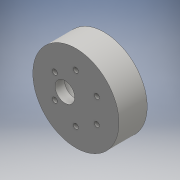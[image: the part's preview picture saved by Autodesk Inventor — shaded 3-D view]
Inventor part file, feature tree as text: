
AUTODESK INVENTOR PART (.ipt)
format: ipt  version: 2016 (Build 200138000, 138)  size: 124,416 bytes
history: native  units: mm
features: extrude x2, sketch x2
ambient origin geometry x8: Origin, YZ Plane, XZ Plane, XY Plane, X Axis, Y Axis, Z Axis, Center Point
bodies: Solid1 (feature_tree)
feature tree (4):
  extrude  "Extrusion1"  Depth=7.0mm
  extrude  "Extrusion2"  Depth=15.5mm
  sketch  "Sketch1"  dims[d0=7.0mm d1=12.5mm]
  sketch  "Sketch2"  dims[d2=3.2mm d3=15.5mm d4=60.0mm d6=360.0deg d8=55.0mm d9=6.0mm d10=0.0mm d11=38.0mm d12=12.0mm d13=0.0mm]
